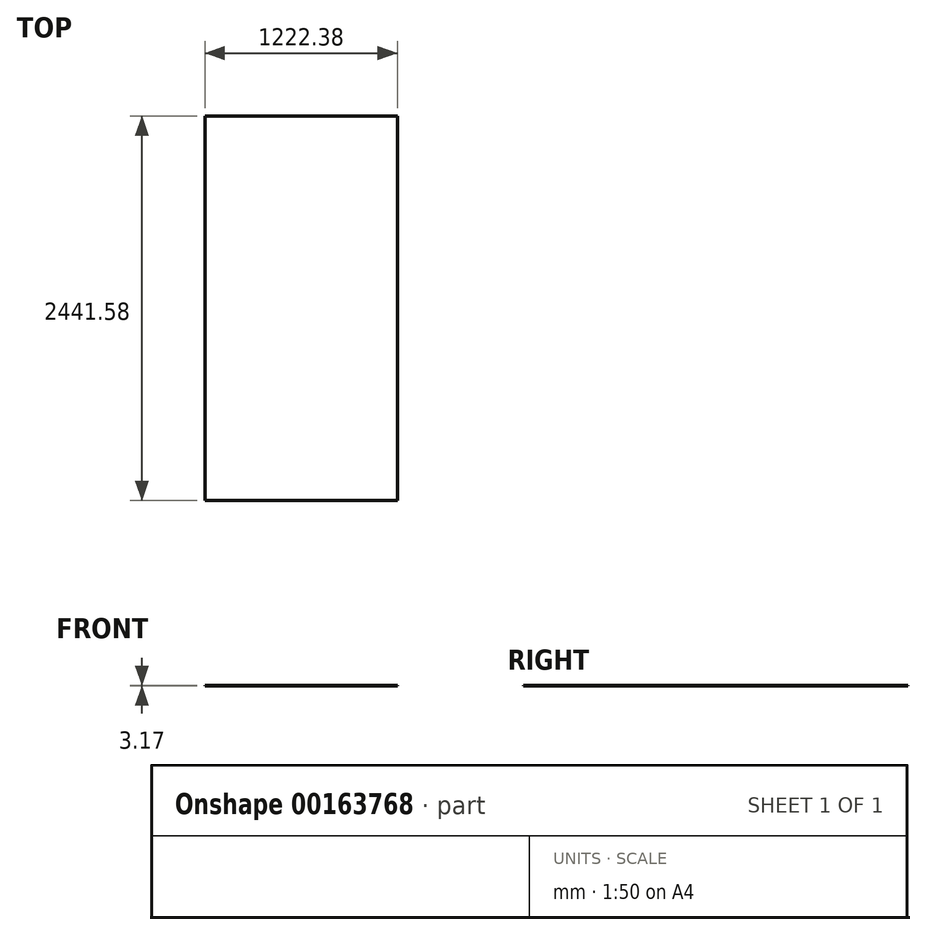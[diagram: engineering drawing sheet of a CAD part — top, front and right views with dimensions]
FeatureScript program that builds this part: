
annotation { "Feature Type Name" : "Feature", "Feature Type Description" : "" }
export const myFeature = defineFeature(function(context is Context, id is Id, definition is map)
    precondition{}
    {
        {
            var Q0;
            Q0=qCreatedBy(makeId("Top.planeOp"),FACE);
            var sketch = newSketch(context, id + "F0", { "sketchPlane" : qUnion([Q0])});
            skLineSegment(sketch, "E0.bottom", {"start": v(611.19, 1220.79) * mm, "end": v(-611.19, 1220.79) * mm});
            skLineSegment(sketch, "E0.top", {"start": v(611.19, -1220.79) * mm, "end": v(-611.19, -1220.79) * mm});
            skLineSegment(sketch, "E0.left", {"start": v(611.19, 1220.79) * mm, "end": v(611.19, -1220.79) * mm});
            skLineSegment(sketch, "E0.right", {"start": v(-611.19, 1220.79) * mm, "end": v(-611.19, -1220.79) * mm});
            skPoint(sketch, "E0.middle", {"position": v(0, 0) * mm});
            skSolve(sketch);
        }
        {
            var Q0;
            Q0 = qSketchRegion(id + "F0", true);
            extrude(context, id + "F1", {"entities" : qUnion([Q0]), "depth" : 3.17 * mm});
        }
    });
